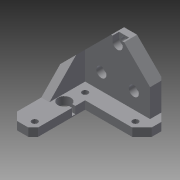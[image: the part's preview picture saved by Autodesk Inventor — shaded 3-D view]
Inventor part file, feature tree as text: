
AUTODESK INVENTOR PART (.ipt)
format: ipt  version: 2015 SP2 (Build 190223200, 223)  size: 146,432 bytes
history: native  units: mm
features: sketch x10, other x3
ambient origin geometry x8: Origin, YZ Plane, XZ Plane, XY Plane, X Axis, Y Axis, Z Axis, Center Point
bodies: Solid1 (feature_tree)
feature tree (13):
  other  "z-axis-bottom.ipt"
  other  "Solid1::z-axis-bottom.ipt"
  other  "TaggingFeature1"
  sketch  "Sketch2"  dims[d0=10.0mm]
  sketch  "Sketch3"
  sketch  "Sketch4"
  sketch  "Sketch6"
  sketch  "Sketch8"
  sketch  "Sketch9"
  sketch  "Sketch10"
  sketch  "Sketch11"
  sketch  "Sketch12"
  sketch  "Sketch13"
